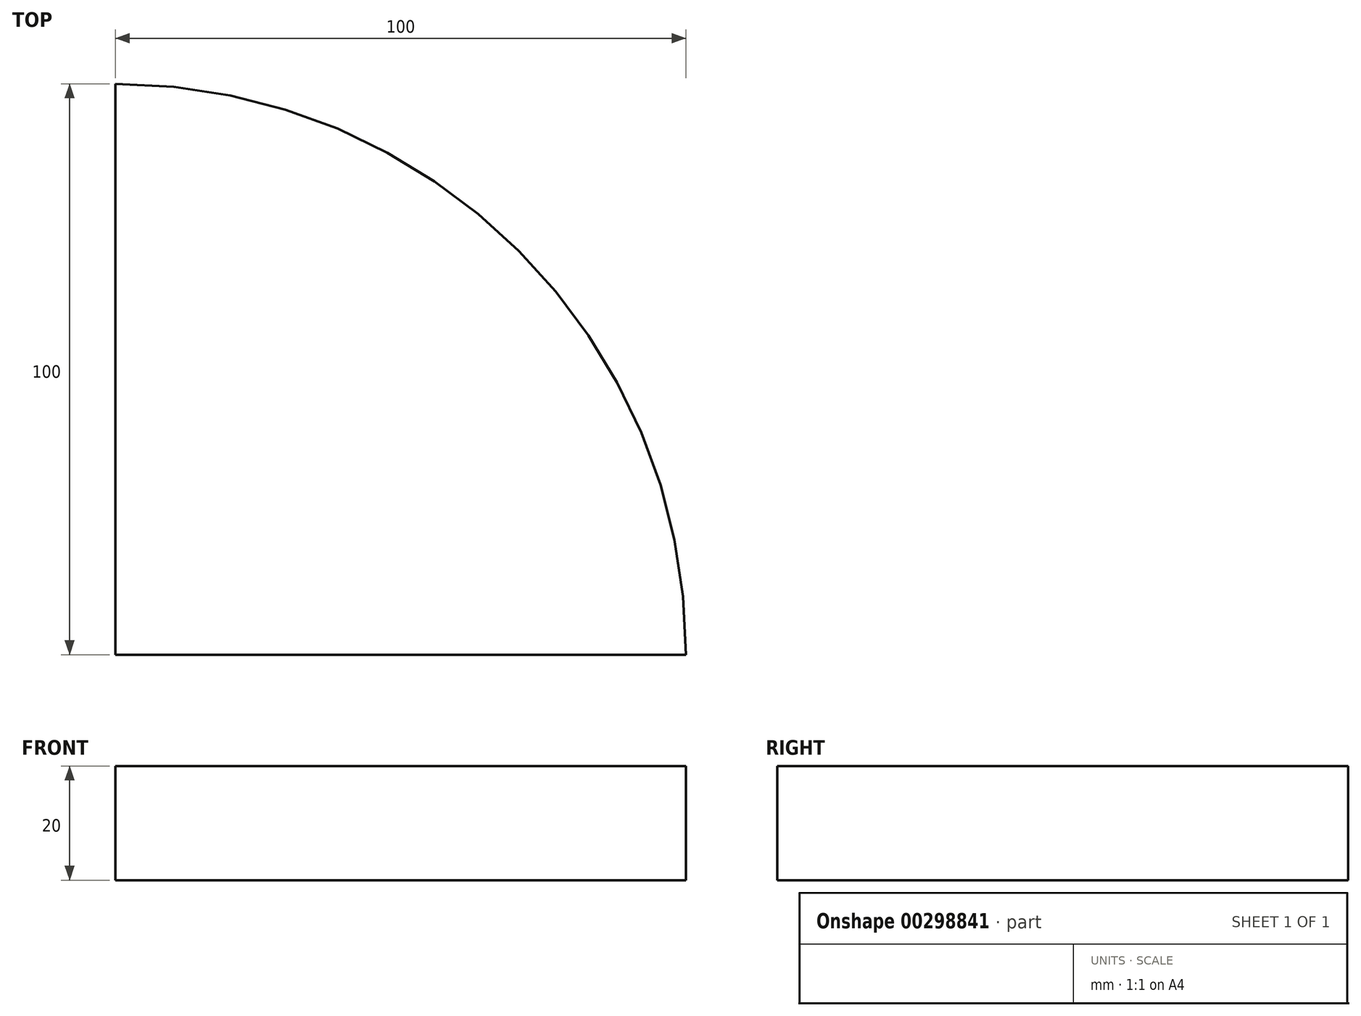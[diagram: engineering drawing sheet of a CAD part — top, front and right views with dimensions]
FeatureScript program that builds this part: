
annotation { "Feature Type Name" : "Feature", "Feature Type Description" : "" }
export const myFeature = defineFeature(function(context is Context, id is Id, definition is map)
    precondition{}
    {
        {
            var Q0;
            Q0=qCreatedBy(makeId("Top.planeOp"),FACE);
            var sketch = newSketch(context, id + "F0", { "sketchPlane" : qUnion([Q0])});
            skLineSegment(sketch, "E0", {"start": v(0, 0) * mm, "end": v(0, 100) * mm});
            skLineSegment(sketch, "E1", {"start": v(0, 0) * mm, "end": v(100, 0) * mm});
            skArc(sketch, "E2", {"start": v(100, 0) * mm, "mid": v(70.71, 70.71) * mm, "end": v(0, 100) * mm});
            skSolve(sketch);
        }
        {
            var Q0;
            Q0=makeQuery(id+"F0.imprint","IMPRINT",FACE,{"disambiguationData":[TD([[makeQuery(id+"F0.imprint","IMPRINT",EDGE,{"derivedFrom":sQuery(id+"F0.wireOp",EDGE,"E0")}),-1.0]])]});
            extrude(context, id + "F1", {"entities" : qUnion([Q0]), "endBound" : BoundingType.SYMMETRIC, "depth" : 20 * mm});
        }
    });
